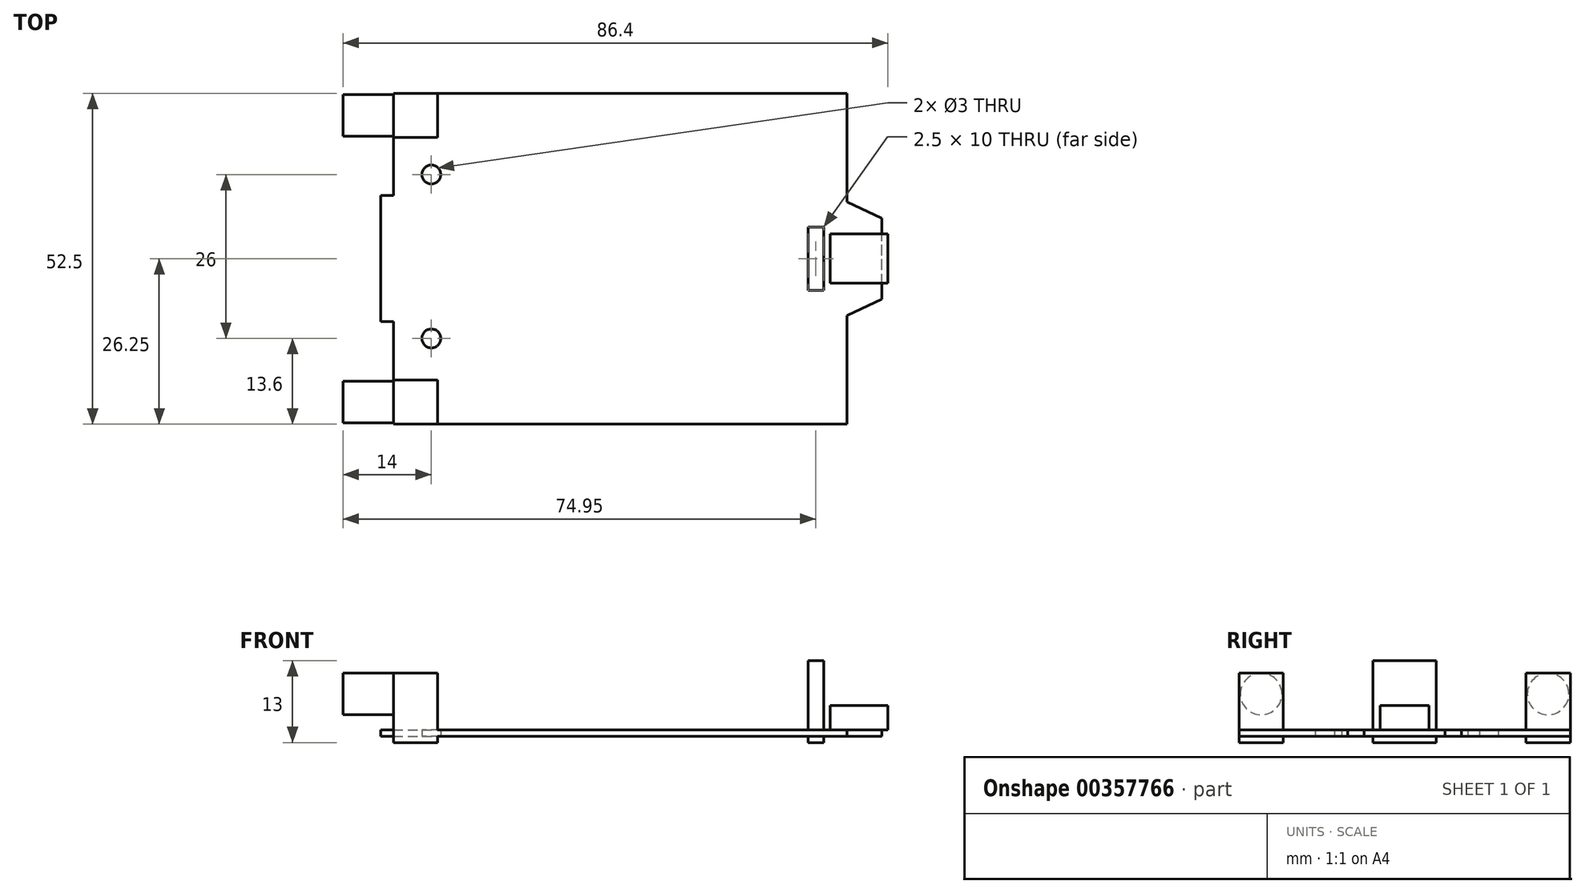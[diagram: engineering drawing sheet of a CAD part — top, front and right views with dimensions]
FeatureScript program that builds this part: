
annotation { "Feature Type Name" : "Feature", "Feature Type Description" : "" }
export const myFeature = defineFeature(function(context is Context, id is Id, definition is map)
    precondition{}
    {
        {
            var Q0;
            Q0=qCreatedBy(makeId("Top.planeOp"),FACE);
            var sketch = newSketch(context, id + "F0", { "sketchPlane" : qUnion([Q0])});
            skLineSegment(sketch, "E0.bottom", {"start": v(0, 0) * mm, "end": v(71.9, 0) * mm});
            skLineSegment(sketch, "E0.top", {"start": v(0, 52.5) * mm, "end": v(71.9, 52.5) * mm});
            skLineSegment(sketch, "E1", {"start": v(-2, 36.25) * mm, "end": v(-2, 16.25) * mm});
            skLineSegment(sketch, "E2", {"start": v(0, 52.5) * mm, "end": v(0, 36.25) * mm});
            skLineSegment(sketch, "E3", {"start": v(0, 16.25) * mm, "end": v(0, 0) * mm});
            skLineSegment(sketch, "E4", {"start": v(0, 36.25) * mm, "end": v(-2, 36.25) * mm});
            skLineSegment(sketch, "E5", {"start": v(0, 16.25) * mm, "end": v(-2, 16.25) * mm});
            skLineSegment(sketch, "E6", {"start": v(71.9, 0) * mm, "end": v(71.9, 17.25) * mm});
            skLineSegment(sketch, "E7", {"start": v(71.9, 17.25) * mm, "end": v(77.4, 19.85) * mm});
            skLineSegment(sketch, "E8", {"start": v(77.4, 19.85) * mm, "end": v(77.4, 32.65) * mm});
            skLineSegment(sketch, "E9", {"start": v(77.4, 32.65) * mm, "end": v(71.9, 35.25) * mm});
            skLineSegment(sketch, "E10", {"start": v(71.9, 35.25) * mm, "end": v(71.9, 52.5) * mm});
            skCircle(sketch, "E11", {"center": v(6, 39.6) * mm, "radius": 1.5 * mm});
            skCircle(sketch, "E12", {"center": v(6, 13.6) * mm, "radius": 1.5 * mm});
            skSolve(sketch);
        }
        {
            var Q0;
            Q0=makeQuery(id+"F0.imprint","IMPRINT",FACE,{"disambiguationData":[TD([[makeQuery(id+"F0.imprint","IMPRINT",EDGE,{"derivedFrom":sQuery(id+"F0.wireOp",EDGE,"E0.bottom")}),1.0]])]});
            extrude(context, id + "F1", {"entities" : qUnion([Q0]), "depth" : 1 * mm});
        }
        {
            var Q0;
            Q0=makeQuery(id+"F1.opExtrude","CAP_FACE",FACE,{"disambiguationData":[OSD([sQuery(id+"F0.wireOp",EDGE,"E0.bottom"),sQuery(id+"F0.wireOp",EDGE,"E0.top"),sQuery(id+"F0.wireOp",EDGE,"E1"),sQuery(id+"F0.wireOp",EDGE,"E2"),sQuery(id+"F0.wireOp",EDGE,"E3"),sQuery(id+"F0.wireOp",EDGE,"E4"),sQuery(id+"F0.wireOp",EDGE,"E5"),sQuery(id+"F0.wireOp",EDGE,"E6"),sQuery(id+"F0.wireOp",EDGE,"E7"),sQuery(id+"F0.wireOp",EDGE,"E8"),sQuery(id+"F0.wireOp",EDGE,"E9"),sQuery(id+"F0.wireOp",EDGE,"E10"),sQuery(id+"F0.wireOp",EDGE,"E11"),sQuery(id+"F0.wireOp",EDGE,"E12")])],"isStart":false});
            var sketch = newSketch(context, id + "F2", { "sketchPlane" : qUnion([Q0])});
            skLineSegment(sketch, "E13.bottom", {"start": v(0, 52.5) * mm, "end": v(7, 52.5) * mm});
            skLineSegment(sketch, "E13.top", {"start": v(0, 45.5) * mm, "end": v(7, 45.5) * mm});
            skLineSegment(sketch, "E13.left", {"start": v(0, 52.5) * mm, "end": v(0, 45.5) * mm});
            skLineSegment(sketch, "E13.right", {"start": v(7, 52.5) * mm, "end": v(7, 45.5) * mm});
            skLineSegment(sketch, "E14.bottom", {"start": v(0, 0) * mm, "end": v(7, 0) * mm});
            skLineSegment(sketch, "E14.top", {"start": v(0, 7) * mm, "end": v(7, 7) * mm});
            skLineSegment(sketch, "E14.left", {"start": v(0, 0) * mm, "end": v(0, 7) * mm});
            skLineSegment(sketch, "E14.right", {"start": v(7, 0) * mm, "end": v(7, 7) * mm});
            skSolve(sketch);
        }
        {
            var Q0;
            Q0 = qSketchRegion(id + "F2", true);
            extrude(context, id + "F3", {"entities" : qUnion([Q0]), "operationType" : NewBodyOperationType.ADD, "oppositeDirection" : true, "depth" : 2 * mm});
        }
        {
            var Q0;
            Q0 = qSketchRegion(id + "F2", true);
            extrude(context, id + "F4", {"entities" : qUnion([Q0]), "operationType" : NewBodyOperationType.ADD, "depth" : 9 * mm});
        }
        {
            var Q0;
            Q0=makeQuery(id+"F4.boolean.opBoolean","MERGE",FACE,{"derivedFrom":[makeQuery(id+"F1.opExtrude","SWEPT_FACE",FACE,{"disambiguationData":[OSD([sQuery(id+"F0.wireOp",EDGE,"E2")])]}),makeQuery(id+"F4.opExtrude","SWEPT_FACE",FACE,{"disambiguationData":[OSD([sQuery(id+"F2.wireOp",EDGE,"E13.left")])]})]});
            var sketch = newSketch(context, id + "F5", { "sketchPlane" : qUnion([Q0])});
            skCircle(sketch, "E15", {"center": v(-49, 6.7) * mm, "radius": 3.3 * mm});
            skPoint(sketch, "E16", {"position": v(-49, 10) * mm});
            skCircle(sketch, "E17", {"center": v(-3.5, 6.7) * mm, "radius": 3.3 * mm});
            skPoint(sketch, "E18.0", {"position": v(-3.5, 10) * mm});
            skSolve(sketch);
        }
        {
            var Q0;
            Q0 = qSketchRegion(id + "F5", true);
            extrude(context, id + "F6", {"entities" : qUnion([Q0]), "operationType" : NewBodyOperationType.ADD, "depth" : 8 * mm});
        }
        {
            var Q0;
            Q0=makeQuery(id+"F1.opExtrude","CAP_FACE",FACE,{"disambiguationData":[OSD([sQuery(id+"F0.wireOp",EDGE,"E0.bottom"),sQuery(id+"F0.wireOp",EDGE,"E0.top"),sQuery(id+"F0.wireOp",EDGE,"E1"),sQuery(id+"F0.wireOp",EDGE,"E2"),sQuery(id+"F0.wireOp",EDGE,"E3"),sQuery(id+"F0.wireOp",EDGE,"E4"),sQuery(id+"F0.wireOp",EDGE,"E5"),sQuery(id+"F0.wireOp",EDGE,"E6"),sQuery(id+"F0.wireOp",EDGE,"E7"),sQuery(id+"F0.wireOp",EDGE,"E8"),sQuery(id+"F0.wireOp",EDGE,"E9"),sQuery(id+"F0.wireOp",EDGE,"E10"),sQuery(id+"F0.wireOp",EDGE,"E11"),sQuery(id+"F0.wireOp",EDGE,"E12")])],"isStart":false});
            var sketch = newSketch(context, id + "F7", { "sketchPlane" : qUnion([Q0])});
            skLineSegment(sketch, "E19.bottom", {"start": v(69.2, 30.15) * mm, "end": v(78.4, 30.15) * mm});
            skLineSegment(sketch, "E19.top", {"start": v(69.2, 22.35) * mm, "end": v(78.4, 22.35) * mm});
            skLineSegment(sketch, "E19.left", {"start": v(69.2, 30.15) * mm, "end": v(69.2, 22.35) * mm});
            skLineSegment(sketch, "E19.right", {"start": v(78.4, 30.15) * mm, "end": v(78.4, 22.35) * mm});
            skPoint(sketch, "E20", {"position": v(77.4, 26.25) * mm});
            skPoint(sketch, "E21", {"position": v(78.4, 26.25) * mm});
            skSolve(sketch);
        }
        {
            var Q0;
            Q0 = qSketchRegion(id + "F7", true);
            extrude(context, id + "F8", {"entities" : qUnion([Q0]), "operationType" : NewBodyOperationType.ADD, "depth" : 3.9 * mm});
        }
        {
            var Q0;
            Q0=makeQuery(id+"F1.opExtrude","CAP_FACE",FACE,{"disambiguationData":[OSD([sQuery(id+"F0.wireOp",EDGE,"E0.bottom"),sQuery(id+"F0.wireOp",EDGE,"E0.top"),sQuery(id+"F0.wireOp",EDGE,"E1"),sQuery(id+"F0.wireOp",EDGE,"E2"),sQuery(id+"F0.wireOp",EDGE,"E3"),sQuery(id+"F0.wireOp",EDGE,"E4"),sQuery(id+"F0.wireOp",EDGE,"E5"),sQuery(id+"F0.wireOp",EDGE,"E6"),sQuery(id+"F0.wireOp",EDGE,"E7"),sQuery(id+"F0.wireOp",EDGE,"E8"),sQuery(id+"F0.wireOp",EDGE,"E9"),sQuery(id+"F0.wireOp",EDGE,"E10"),sQuery(id+"F0.wireOp",EDGE,"E11"),sQuery(id+"F0.wireOp",EDGE,"E12")])],"isStart":false});
            var sketch = newSketch(context, id + "F9", { "sketchPlane" : qUnion([Q0])});
            skLineSegment(sketch, "E22.bottom", {"start": v(65.7, 31.25) * mm, "end": v(68.2, 31.25) * mm});
            skLineSegment(sketch, "E22.top", {"start": v(65.7, 21.25) * mm, "end": v(68.2, 21.25) * mm});
            skLineSegment(sketch, "E22.left", {"start": v(65.7, 31.25) * mm, "end": v(65.7, 21.25) * mm});
            skLineSegment(sketch, "E22.right", {"start": v(68.2, 31.25) * mm, "end": v(68.2, 21.25) * mm});
            skPoint(sketch, "E23", {"position": v(68.2, 26.25) * mm});
            skPoint(sketch, "E24", {"position": v(69.2, 26.25) * mm});
            skSolve(sketch);
        }
        {
            var Q0;
            Q0=makeQuery(id+"F9.imprint","IMPRINT",FACE,{"disambiguationData":[TD([[makeQuery(id+"F9.imprint","IMPRINT",EDGE,{"derivedFrom":sQuery(id+"F9.wireOp",EDGE,"E22.bottom")}),-1.0]])]});
            extrude(context, id + "F10", {"entities" : qUnion([Q0]), "operationType" : NewBodyOperationType.ADD, "oppositeDirection" : true, "depth" : 2 * mm});
        }
        {
            var Q0;
            Q0=makeQuery(id+"F9.imprint","IMPRINT",FACE,{"disambiguationData":[TD([[makeQuery(id+"F9.imprint","IMPRINT",EDGE,{"derivedFrom":sQuery(id+"F9.wireOp",EDGE,"E22.bottom")}),-1.0]])]});
            extrude(context, id + "F11", {"entities" : qUnion([Q0]), "operationType" : NewBodyOperationType.ADD, "depth" : 11 * mm});
        }
    });
